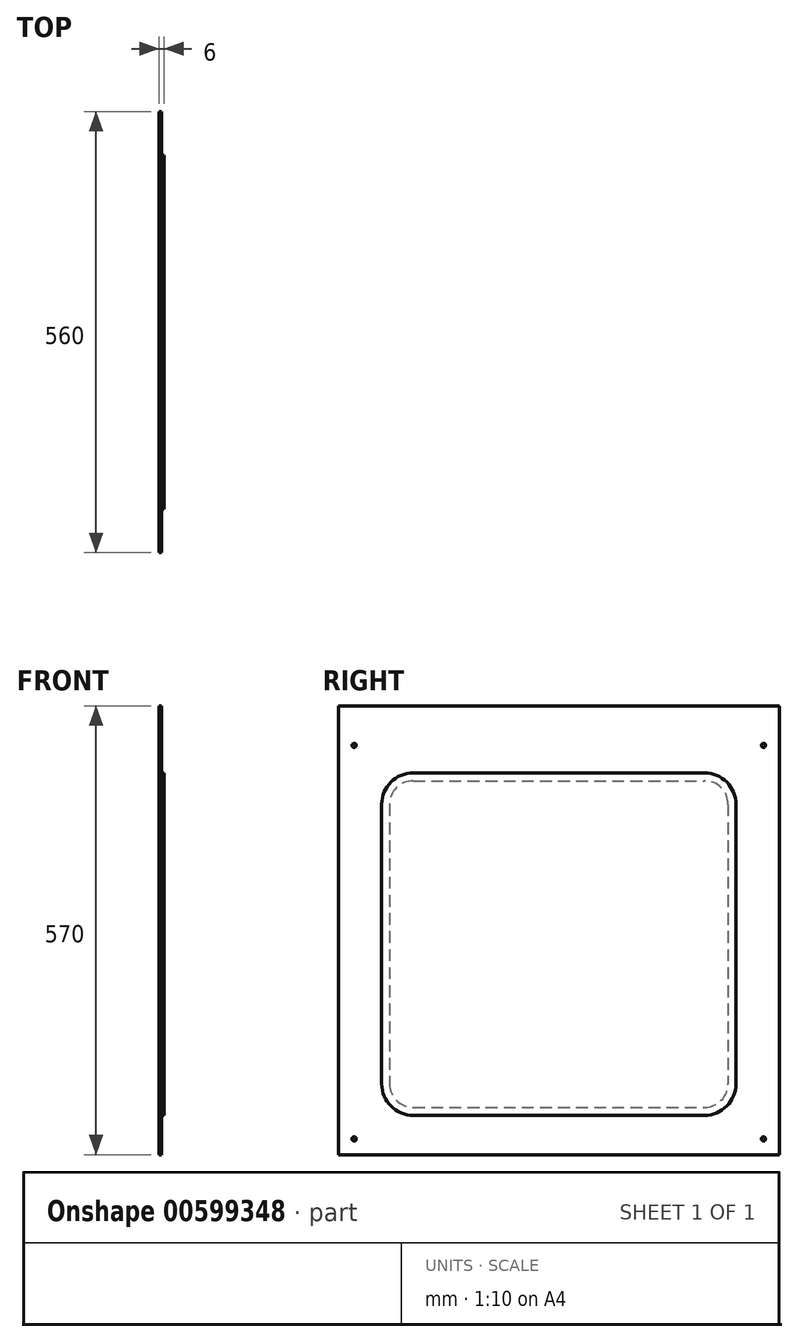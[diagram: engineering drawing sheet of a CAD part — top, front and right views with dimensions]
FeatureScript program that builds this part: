
annotation { "Feature Type Name" : "Feature", "Feature Type Description" : "" }
export const myFeature = defineFeature(function(context is Context, id is Id, definition is map)
    precondition{}
    {
        {
            var Q0;
            Q0=qCreatedBy(makeId("Right.planeOp"),FACE);
            var sketch = newSketch(context, id + "F0", { "sketchPlane" : qUnion([Q0])});
            skLineSegment(sketch, "E0.bottom", {"start": v(-270, 260) * mm, "end": v(270, 260) * mm});
            skLineSegment(sketch, "E0.top", {"start": v(-270, -260) * mm, "end": v(270, -260) * mm, "construction": true});
            skLineSegment(sketch, "E0.left", {"start": v(-270, 260) * mm, "end": v(-270, -260) * mm});
            skLineSegment(sketch, "E0.right", {"start": v(270, 260) * mm, "end": v(270, -260) * mm, "construction": true});
            skCircle(sketch, "E1", {"center": v(-260, 250) * mm, "radius": 2.65 * mm});
            skCircle(sketch, "E2", {"center": v(-260, -250) * mm, "radius": 2.65 * mm});
            skCircle(sketch, "E3", {"center": v(260, -250) * mm, "radius": 2.65 * mm});
            skCircle(sketch, "E4", {"center": v(260, 250) * mm, "radius": 2.65 * mm});
            skLineSegment(sketch, "E5.bottom", {"start": v(-270, 260) * mm, "end": v(270, 260) * mm, "construction": true});
            skLineSegment(sketch, "E5.top", {"start": v(-270, 300) * mm, "end": v(270, 300) * mm});
            skLineSegment(sketch, "E5.left", {"start": v(-270, 260) * mm, "end": v(-270, 300) * mm});
            skLineSegment(sketch, "E5.right", {"start": v(270, 260) * mm, "end": v(270, 300) * mm, "construction": true});
            skLineSegment(sketch, "E6.bottom", {"start": v(270, -260) * mm, "end": v(280, -260) * mm, "construction": true});
            skLineSegment(sketch, "E6.top", {"start": v(270, 300) * mm, "end": v(280, 300) * mm});
            skLineSegment(sketch, "E6.left", {"start": v(270, -260) * mm, "end": v(270, 300) * mm});
            skLineSegment(sketch, "E6.right", {"start": v(280, -260) * mm, "end": v(280, 300) * mm});
            skLineSegment(sketch, "E7.bottom", {"start": v(-270, -260) * mm, "end": v(-280, -260) * mm, "construction": true});
            skLineSegment(sketch, "E7.top", {"start": v(-270, 300) * mm, "end": v(-280, 300) * mm});
            skLineSegment(sketch, "E7.left", {"start": v(-270, -260) * mm, "end": v(-270, 300) * mm, "construction": true});
            skLineSegment(sketch, "E7.right", {"start": v(-280, -260) * mm, "end": v(-280, 300) * mm});
            skLineSegment(sketch, "E8.bottom", {"start": v(-215, 205) * mm, "end": v(215, 205) * mm});
            skLineSegment(sketch, "E8.top", {"start": v(-215, -210) * mm, "end": v(215, -210) * mm});
            skLineSegment(sketch, "E8.left", {"start": v(-215, 205) * mm, "end": v(-215, -210) * mm});
            skLineSegment(sketch, "E8.right", {"start": v(215, 205) * mm, "end": v(215, -210) * mm});
            skLineSegment(sketch, "E9", {"start": v(-280, -260) * mm, "end": v(-280, -270) * mm});
            skLineSegment(sketch, "E10", {"start": v(-280, -270) * mm, "end": v(280, -270) * mm});
            skLineSegment(sketch, "E11", {"start": v(280, -270) * mm, "end": v(280, -260) * mm});
            skSolve(sketch);
        }
        {
            var Q0;
            Q0=qSketchRegion(id+"F0",true);
            extrude(context, id + "F1", {"entities" : qUnion([Q0]), "depth" : 3 * mm});
        }
        {
            var Q0;
            Q0=makeQuery(id+"F1.opExtrude","SWEPT_EDGE",EDGE,{"disambiguationData":[OSD([sQuery(id+"F0.wireOp",EDGE,"E8.bottom"),sQuery(id+"F0.wireOp",EDGE,"E8.left")])]});
            var Q1;
            Q1=makeQuery(id+"F1.opExtrude","SWEPT_EDGE",EDGE,{"disambiguationData":[OSD([sQuery(id+"F0.wireOp",EDGE,"E8.bottom"),sQuery(id+"F0.wireOp",EDGE,"E8.right")])]});
            var Q2;
            Q2=makeQuery(id+"F1.opExtrude","SWEPT_EDGE",EDGE,{"disambiguationData":[OSD([sQuery(id+"F0.wireOp",EDGE,"E8.top"),sQuery(id+"F0.wireOp",EDGE,"E8.right")])]});
            var Q3;
            Q3=makeQuery(id+"F1.opExtrude","SWEPT_EDGE",EDGE,{"disambiguationData":[OSD([sQuery(id+"F0.wireOp",EDGE,"E8.top"),sQuery(id+"F0.wireOp",EDGE,"E8.left")])]});
            fillet(context, id + "F2", {"entities" : qUnion([Q0, Q1, Q2, Q3]), "radius" : 30 * mm, "tangentPropagation" : true, "allowEdgeOverflow" : false});
        }
        {
            var Q0;
            Q0=makeQuery(id+"F1.opExtrude","CAP_FACE",FACE,{"disambiguationData":[OSD([sQuery(id+"F0.wireOp",EDGE,"E0.top"),sQuery(id+"F0.wireOp",EDGE,"E1"),sQuery(id+"F0.wireOp",EDGE,"E2"),sQuery(id+"F0.wireOp",EDGE,"E3"),sQuery(id+"F0.wireOp",EDGE,"E4"),sQuery(id+"F0.wireOp",EDGE,"E5.top"),sQuery(id+"F0.wireOp",EDGE,"E6.bottom"),sQuery(id+"F0.wireOp",EDGE,"E6.top"),sQuery(id+"F0.wireOp",EDGE,"E6.right"),sQuery(id+"F0.wireOp",EDGE,"E7.bottom"),sQuery(id+"F0.wireOp",EDGE,"E7.top"),sQuery(id+"F0.wireOp",EDGE,"E7.right"),sQuery(id+"F0.wireOp",EDGE,"E8.bottom"),sQuery(id+"F0.wireOp",EDGE,"E8.top"),sQuery(id+"F0.wireOp",EDGE,"E8.left"),sQuery(id+"F0.wireOp",EDGE,"E8.right")])],"isStart":false});
            var sketch = newSketch(context, id + "F3", { "sketchPlane" : qUnion([Q0])});
            skLineSegment(sketch, "E12.0", {"start": v(-280, 300) * mm, "end": v(-280, 300) * mm});
            skLineSegment(sketch, "E13.0", {"start": v(-185, -210) * mm, "end": v(185, -210) * mm, "construction": true});
            skArc(sketch, "E14.0", {"start": v(215, -180) * mm, "mid": v(206.21, -201.21) * mm, "end": v(185, -210) * mm, "construction": true});
            skLineSegment(sketch, "E15.0", {"start": v(215, 175) * mm, "end": v(215, -180) * mm, "construction": true});
            skArc(sketch, "E16.0", {"start": v(185, 205) * mm, "mid": v(206.21, 196.21) * mm, "end": v(215, 175) * mm, "construction": true});
            skLineSegment(sketch, "E17.0", {"start": v(-185, 205) * mm, "end": v(185, 205) * mm, "construction": true});
            skLineSegment(sketch, "E18.0", {"start": v(-215, 175) * mm, "end": v(-215, -180) * mm, "construction": true});
            skArc(sketch, "E19.0", {"start": v(-185, -210) * mm, "mid": v(-206.21, -201.21) * mm, "end": v(-215, -180) * mm, "construction": true});
            skArc(sketch, "E20.0", {"start": v(-215, 175) * mm, "mid": v(-206.21, 196.21) * mm, "end": v(-185, 205) * mm, "construction": true});
            skLineSegment(sketch, "E21.0", {"start": v(-185, -220) * mm, "end": v(185, -220) * mm});
            skArc(sketch, "E21.1", {"start": v(225, -180) * mm, "mid": v(213.28, -208.28) * mm, "end": v(185, -220) * mm});
            skArc(sketch, "E21.2", {"start": v(-185, -220) * mm, "mid": v(-213.28, -208.28) * mm, "end": v(-225, -180) * mm});
            skLineSegment(sketch, "E21.3", {"start": v(225, 175) * mm, "end": v(225, -180) * mm});
            skLineSegment(sketch, "E21.4", {"start": v(-225, 175) * mm, "end": v(-225, -180) * mm});
            skArc(sketch, "E21.5", {"start": v(-225, 175) * mm, "mid": v(-213.28, 203.28) * mm, "end": v(-185, 215) * mm});
            skLineSegment(sketch, "E21.6", {"start": v(-185, 215) * mm, "end": v(185, 215) * mm});
            skArc(sketch, "E21.7", {"start": v(185, 215) * mm, "mid": v(213.28, 203.28) * mm, "end": v(225, 175) * mm});
            skSolve(sketch);
        }
        {
            var Q0;
            Q0=qSketchRegion(id+"F3",true);
            extrude(context, id + "F4", {"entities" : qUnion([Q0]), "depth" : 3 * mm});
        }
    });
